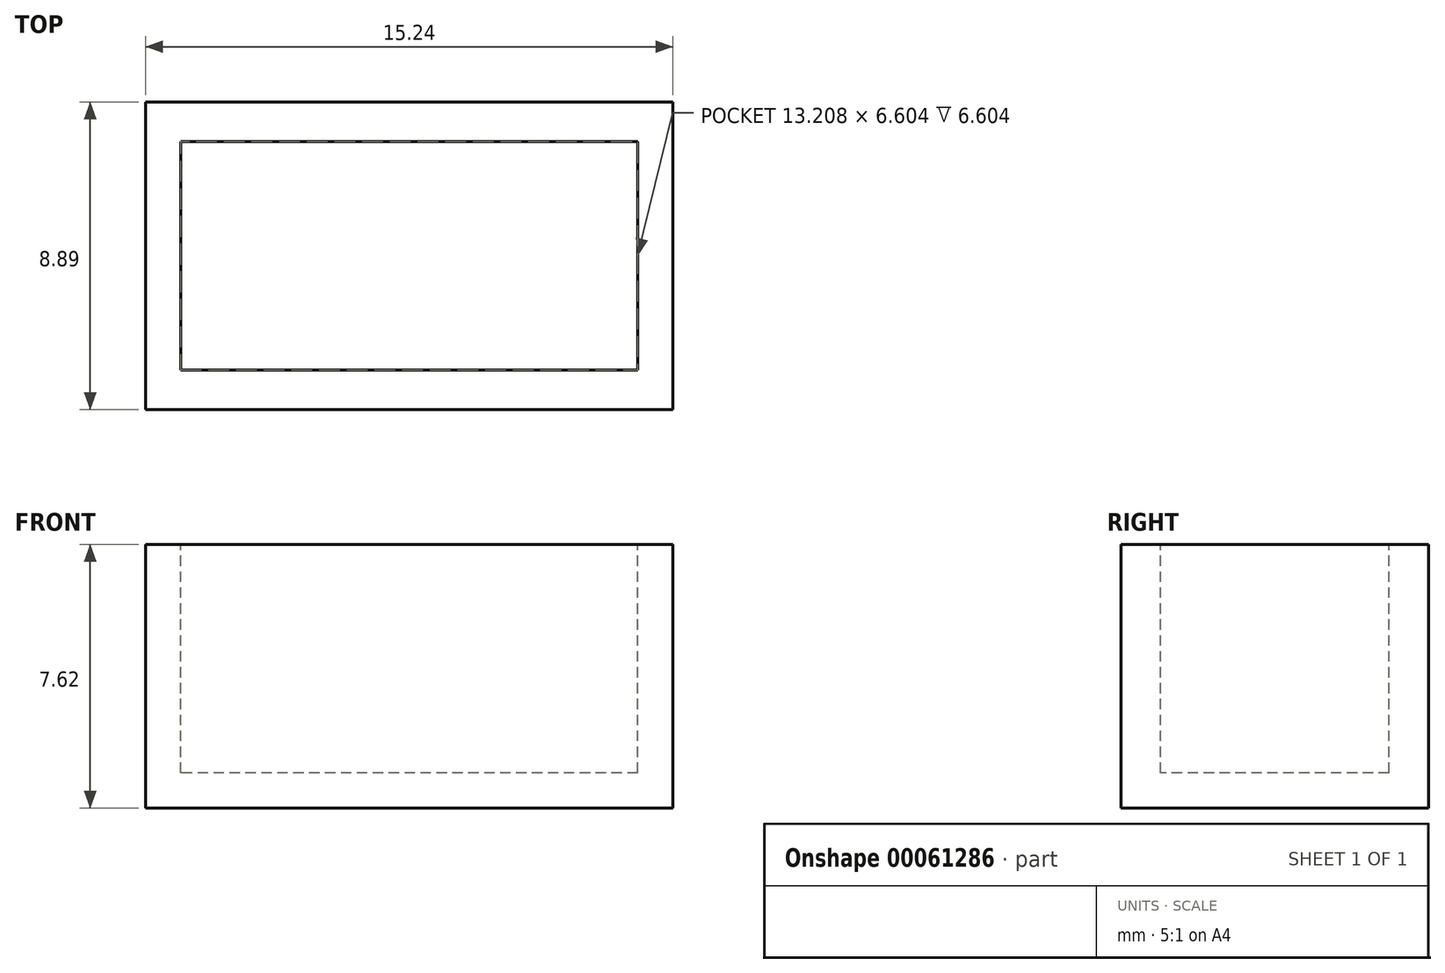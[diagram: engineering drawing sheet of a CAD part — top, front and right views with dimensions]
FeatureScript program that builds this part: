
annotation { "Feature Type Name" : "Feature", "Feature Type Description" : "" }
export const myFeature = defineFeature(function(context is Context, id is Id, definition is map)
    precondition{}
    {
        {
            var Q0;
            Q0=qCreatedBy(makeId("Front.planeOp"),FACE);
            var sketch = newSketch(context, id + "F0", { "sketchPlane" : qUnion([Q0])});
            skLineSegment(sketch, "E0.bottom", {"start": v(-38.04, 42.82) * mm, "end": v(-22.8, 42.82) * mm});
            skLineSegment(sketch, "E0.top", {"start": v(-38.04, 35.2) * mm, "end": v(-22.8, 35.2) * mm});
            skLineSegment(sketch, "E0.left", {"start": v(-38.04, 42.82) * mm, "end": v(-38.04, 35.2) * mm});
            skLineSegment(sketch, "E0.right", {"start": v(-22.8, 42.82) * mm, "end": v(-22.8, 35.2) * mm});
            skSolve(sketch);
        }
        {
            var Q0;
            Q0=makeQuery(id+"F0.imprint","IMPRINT",FACE,{"disambiguationData":[TD([[makeQuery(id+"F0.imprint","IMPRINT",EDGE,{"derivedFrom":sQuery(id+"F0.wireOp",EDGE,"E0.bottom")}),-1.0]])]});
            extrude(context, id + "F1", {"entities" : qUnion([Q0]), "depth" : 8.9 * mm});
        }
        {
            var Q0;
            Q0=makeQuery(id+"F1.opExtrude","SWEPT_FACE",FACE,{"disambiguationData":[OSD([sQuery(id+"F0.wireOp",EDGE,"E0.bottom")])]});
            var sketch = newSketch(context, id + "F2", { "sketchPlane" : qUnion([Q0])});
            skLineSegment(sketch, "E1.bottom", {"start": v(-23.81, -1.14) * mm, "end": v(-37.02, -1.14) * mm});
            skLineSegment(sketch, "E1.top", {"start": v(-23.81, -7.75) * mm, "end": v(-37.02, -7.75) * mm});
            skLineSegment(sketch, "E1.left", {"start": v(-23.81, -1.14) * mm, "end": v(-23.81, -7.75) * mm});
            skLineSegment(sketch, "E1.right", {"start": v(-37.02, -1.14) * mm, "end": v(-37.02, -7.75) * mm});
            skSolve(sketch);
        }
        {
            var Q0;
            Q0=makeQuery(id+"F2.imprint","IMPRINT",FACE,{"disambiguationData":[TD([[makeQuery(id+"F2.imprint","IMPRINT",EDGE,{"derivedFrom":sQuery(id+"F2.wireOp",EDGE,"E1.bottom")}),1.0]])]});
            extrude(context, id + "F3", {"entities" : qUnion([Q0]), "operationType" : NewBodyOperationType.REMOVE, "oppositeDirection" : true, "depth" : 6.6 * mm});
        }
    });
